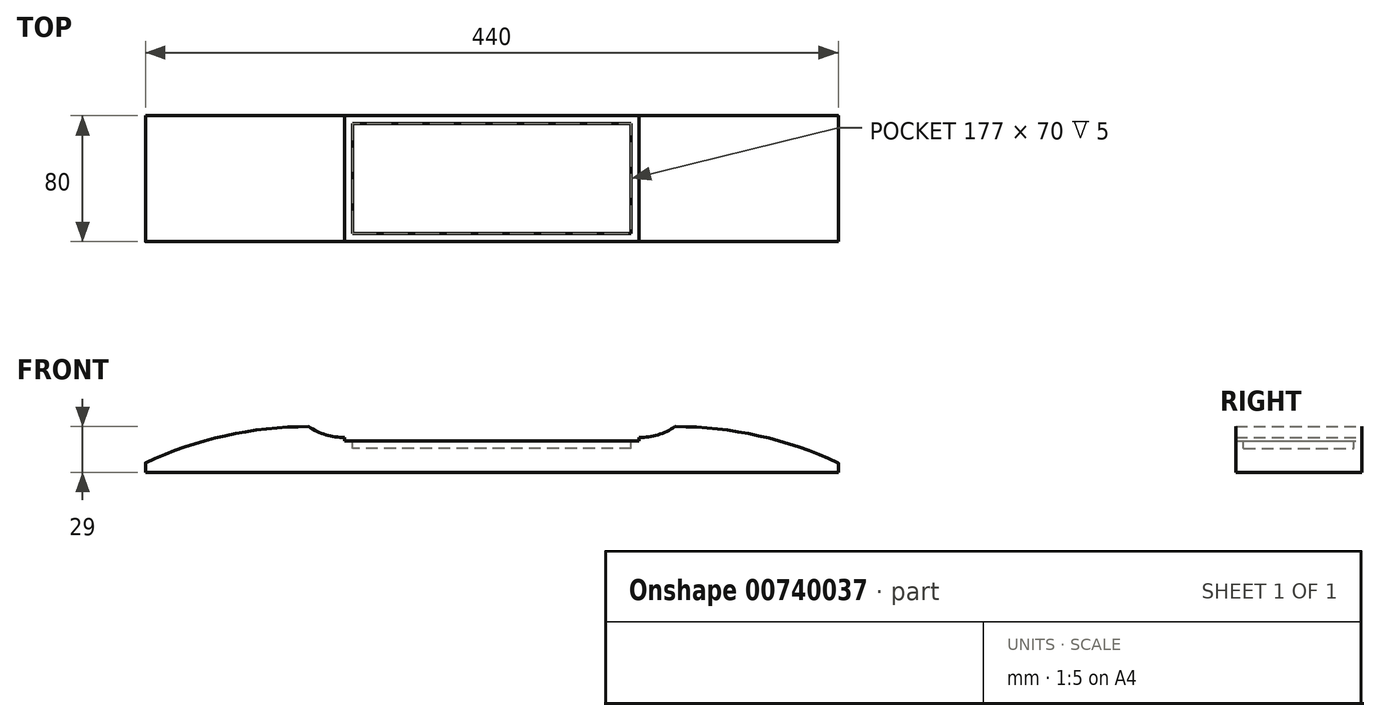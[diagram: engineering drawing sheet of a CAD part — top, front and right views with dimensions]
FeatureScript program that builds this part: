
annotation { "Feature Type Name" : "Feature", "Feature Type Description" : "" }
export const myFeature = defineFeature(function(context is Context, id is Id, definition is map)
    precondition{}
    {
        {
            var Q0;
            Q0=qCreatedBy(makeId("Front.planeOp"),FACE);
            var sketch = newSketch(context, id + "F0", { "sketchPlane" : qUnion([Q0])});
            skLineSegment(sketch, "E0", {"start": v(0, 0) * mm, "end": v(220, 0) * mm});
            skLineSegment(sketch, "E1", {"start": v(0, 0) * mm, "end": v(-220, 0) * mm});
            skArc(sketch, "E2", {"start": v(93.5, 22) * mm, "mid": v(105.44, 23.78) * mm, "end": v(116.35, 28.97) * mm});
            skArc(sketch, "E3", {"start": v(-116.35, 28.97) * mm, "mid": v(-105.44, 23.78) * mm, "end": v(-93.5, 22) * mm});
            skLineSegment(sketch, "E4", {"start": v(-220, 0) * mm, "end": v(-220, 5.87) * mm});
            skLineSegment(sketch, "E5", {"start": v(220, 0) * mm, "end": v(220, 5.87) * mm});
            skArc(sketch, "E6", {"start": v(-116.46, 29) * mm, "mid": v(-169.43, 23.19) * mm, "end": v(-219.88, 6.05) * mm});
            skArc(sketch, "E7", {"start": v(219.88, 6.05) * mm, "mid": v(169.43, 23.19) * mm, "end": v(116.46, 29) * mm});
            skLineSegment(sketch, "E8", {"start": v(93.5, 20) * mm, "end": v(93.5, 22) * mm});
            skLineSegment(sketch, "E9", {"start": v(-93.5, 20) * mm, "end": v(-93.5, 22) * mm});
            skLineSegment(sketch, "E10", {"start": v(93.5, 20) * mm, "end": v(0, 20) * mm});
            skLineSegment(sketch, "E11", {"start": v(-93.5, 20) * mm, "end": v(0, 20) * mm});
            skArc(sketch, "E12", {"start": v(220, 5.87) * mm, "mid": v(219.97, 5.98) * mm, "end": v(219.88, 6.05) * mm});
            skArc(sketch, "E13", {"start": v(-219.88, 6.05) * mm, "mid": v(-219.97, 5.98) * mm, "end": v(-220, 5.87) * mm});
            skArc(sketch, "E14", {"start": v(116.46, 29) * mm, "mid": v(116.4, 29) * mm, "end": v(116.35, 28.97) * mm});
            skArc(sketch, "E15", {"start": v(-116.35, 28.97) * mm, "mid": v(-116.4, 29) * mm, "end": v(-116.46, 29) * mm});
            skSolve(sketch);
        }
        {
            var Q0;
            Q0=makeQuery(id+"F0.imprint","IMPRINT",FACE,{"disambiguationData":[TD([[makeQuery(id+"F0.imprint","IMPRINT",EDGE,{"derivedFrom":sQuery(id+"F0.wireOp",EDGE,"E0")}),1.0]])]});
            extrude(context, id + "F1", {"entities" : qUnion([Q0]), "depth" : 80 * mm, "offsetDistance" : 25.4 * mm});
        }
        {
            var Q0;
            Q0=makeQuery(id+"F1.opExtrude","SWEPT_FACE",FACE,{"disambiguationData":[OSD([sQuery(id+"F0.wireOp",EDGE,"E10"),sQuery(id+"F0.wireOp",EDGE,"E11")])]});
            var sketch = newSketch(context, id + "F2", { "sketchPlane" : qUnion([Q0])});
            skLineSegment(sketch, "E16.bottom", {"start": v(-30, -25) * mm, "end": v(30, -25) * mm});
            skLineSegment(sketch, "E16.top", {"start": v(-30, -55) * mm, "end": v(30, -55) * mm});
            skLineSegment(sketch, "E16.left", {"start": v(-30, -25) * mm, "end": v(-30, -55) * mm});
            skLineSegment(sketch, "E16.right", {"start": v(30, -25) * mm, "end": v(30, -55) * mm});
            skSolve(sketch);
        }
        {
            var Q0;
            Q0=makeQuery(id+"F1.opExtrude","SWEPT_FACE",FACE,{"disambiguationData":[OSD([sQuery(id+"F0.wireOp",EDGE,"E10"),sQuery(id+"F0.wireOp",EDGE,"E11")])]});
            var sketch = newSketch(context, id + "F3", { "sketchPlane" : qUnion([Q0])});
            skLineSegment(sketch, "E17.bottom", {"start": v(88.5, -75) * mm, "end": v(-88.5, -75) * mm});
            skLineSegment(sketch, "E17.top", {"start": v(88.5, -5) * mm, "end": v(-88.5, -5) * mm});
            skLineSegment(sketch, "E17.left", {"start": v(88.5, -75) * mm, "end": v(88.5, -5) * mm});
            skLineSegment(sketch, "E17.right", {"start": v(-88.5, -75) * mm, "end": v(-88.5, -5) * mm});
            skSolve(sketch);
        }
        {
            var Q0;
            Q0=makeQuery(id+"F3.imprint","IMPRINT",FACE,{"disambiguationData":[TD([[makeQuery(id+"F3.imprint","IMPRINT",EDGE,{"derivedFrom":makeQuery(id+"FEZIENOtiVF92hS_1.boolean.opBoolean","COPY",EDGE,{"derivedFrom":makeQuery(id+"FEZIENOtiVF92hS_1.opExtrude","CAP_EDGE",EDGE,{"disambiguationData":[OSD([sQuery(id+"F2.wireOp",EDGE,"E16.bottom")])],"isStart":true})})}),-1.0]])]});
            var Q1;
            Q1=makeQuery(id+"F3.imprint","IMPRINT",FACE,{"disambiguationData":[TD([[makeQuery(id+"F3.imprint","IMPRINT",EDGE,{"derivedFrom":sQuery(id+"F3.wireOp",EDGE,"E17.bottom")}),-1.0]])]});
            extrude(context, id + "F4", {"entities" : qUnion([Q0, Q1]), "operationType" : NewBodyOperationType.REMOVE, "oppositeDirection" : true, "depth" : 5 * mm, "offsetDistance" : 25.4 * mm});
        }
    });
